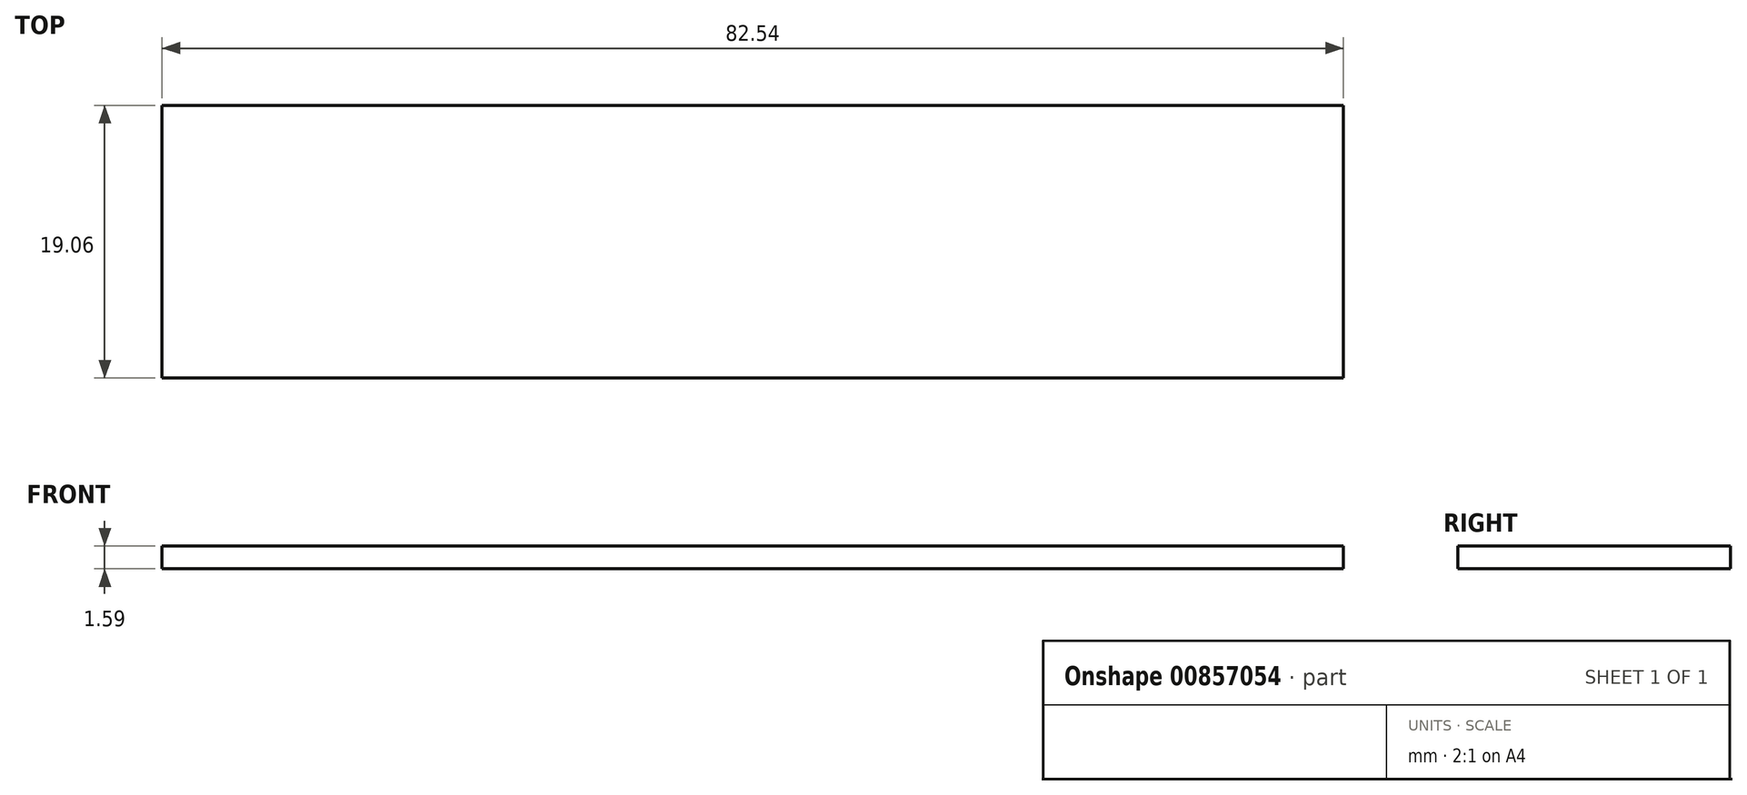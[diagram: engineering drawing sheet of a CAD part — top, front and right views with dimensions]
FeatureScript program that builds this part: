
annotation { "Feature Type Name" : "Feature", "Feature Type Description" : "" }
export const myFeature = defineFeature(function(context is Context, id is Id, definition is map)
    precondition{}
    {
        {
            var Q0;
            Q0=qCreatedBy(makeId("Top.planeOp"),FACE);
            var sketch = newSketch(context, id + "F0", { "sketchPlane" : qUnion([Q0])});
            skLineSegment(sketch, "E0.bottom", {"start": v(-41.28, 9.53) * mm, "end": v(41.28, 9.53) * mm});
            skLineSegment(sketch, "E0.top", {"start": v(-41.28, -9.53) * mm, "end": v(41.27, -9.53) * mm});
            skLineSegment(sketch, "E0.left", {"start": v(-41.28, 9.53) * mm, "end": v(-41.28, -9.53) * mm});
            skLineSegment(sketch, "E0.right", {"start": v(41.28, 9.53) * mm, "end": v(41.27, -9.53) * mm});
            skPoint(sketch, "E0.middle", {"position": v(0, 0) * mm});
            skSolve(sketch);
        }
        {
            var Q0;
            Q0=qSketchRegion(id+"F0",true);
            extrude(context, id + "F1", {"entities" : qUnion([Q0]), "depth" : 1.59 * mm, "offsetDistance" : 25.4 * mm});
        }
    });
